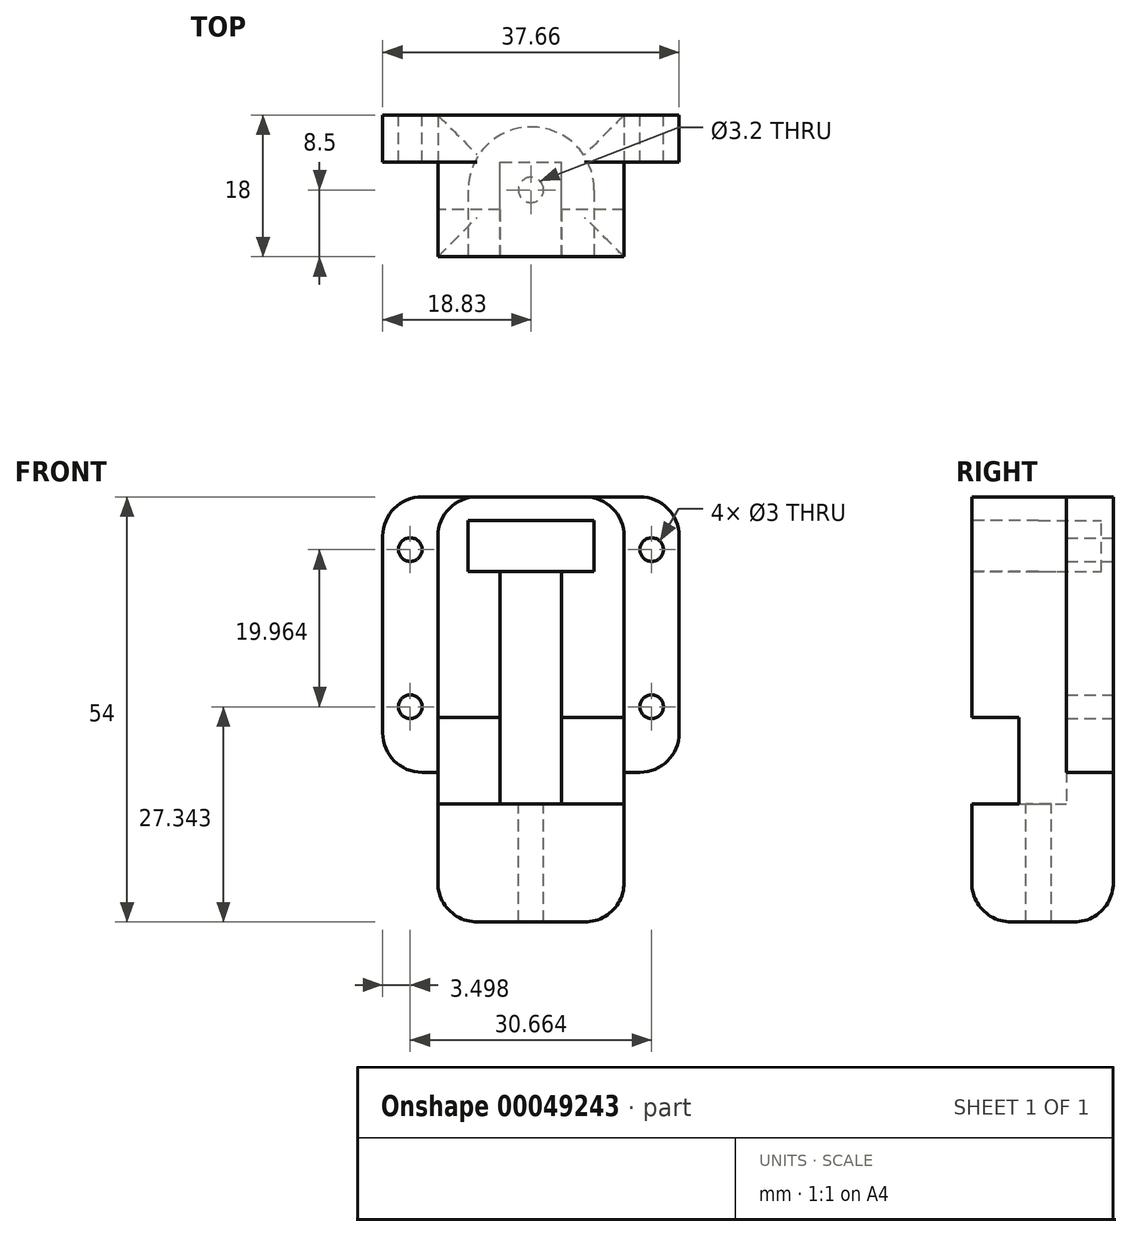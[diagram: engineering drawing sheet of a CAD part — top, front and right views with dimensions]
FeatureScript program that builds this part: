
annotation { "Feature Type Name" : "Feature", "Feature Type Description" : "" }
export const myFeature = defineFeature(function(context is Context, id is Id, definition is map)
    precondition{}
    {
        {
            var Q0;
            Q0=qCreatedBy(makeId("Top.planeOp"),FACE);
            var sketch = newSketch(context, id + "F0", { "sketchPlane" : qUnion([Q0])});
            skPoint(sketch, "E0.middle", {"position": v(0, -5.68) * mm});
            skLineSegment(sketch, "E1", {"start": v(-11.83, 0) * mm, "end": v(-11.83, -2.68) * mm});
            skLineSegment(sketch, "E2", {"start": v(-11.83, -12) * mm, "end": v(-3.9, -12) * mm});
            skLineSegment(sketch, "E3", {"start": v(-3.9, -12) * mm, "end": v(-3.9, 0) * mm});
            skLineSegment(sketch, "E4", {"start": v(-3.9, 0) * mm, "end": v(0, 0) * mm});
            skLineSegment(sketch, "E5", {"start": v(0, 6) * mm, "end": v(-11.84, 6) * mm});
            skLineSegment(sketch, "E6", {"start": v(-11.83, -2.68) * mm, "end": v(-11.83, -12) * mm});
            skLineSegment(sketch, "E7", {"start": v(-11.83, 0) * mm, "end": v(-11.83, 6) * mm});
            skLineSegment(sketch, "E8.MirrorCS", {"start": v(0, 6) * mm, "end": v(11.84, 6) * mm});
            skLineSegment(sketch, "E9.MirrorCS", {"start": v(11.83, 0) * mm, "end": v(11.83, 6) * mm});
            skLineSegment(sketch, "E10.MirrorCS", {"start": v(11.83, 0) * mm, "end": v(11.83, -2.68) * mm});
            skLineSegment(sketch, "E11.MirrorCS", {"start": v(11.83, -2.68) * mm, "end": v(11.83, -12) * mm});
            skLineSegment(sketch, "E12.MirrorCS", {"start": v(11.83, -12) * mm, "end": v(3.9, -12) * mm});
            skLineSegment(sketch, "E13.MirrorCS", {"start": v(3.9, -12) * mm, "end": v(3.9, 0) * mm});
            skLineSegment(sketch, "E14.MirrorCS", {"start": v(3.9, 0) * mm, "end": v(0, 0) * mm});
            skSolve(sketch);
        }
        {
            var Q0;
            Q0=makeQuery(id+"F0.imprint","IMPRINT",FACE,{"disambiguationData":[TD([[makeQuery(id+"F0.imprint","IMPRINT",EDGE,{"derivedFrom":sQuery(id+"F0.wireOp",EDGE,"E1")}),1.0]])]});
            extrude(context, id + "F1", {"entities" : qUnion([Q0]), "depth" : 39 * mm, "hasSecondDirection" : true, "secondDirectionOppositeDirection" : true, "secondDirectionDepth" : 15 * mm});
        }
        {
            var Q0;
            Q0=qCreatedBy(makeId("Top.planeOp"),FACE);
            var sketch = newSketch(context, id + "F2", { "sketchPlane" : qUnion([Q0])});
            skLineSegment(sketch, "E15.bottom", {"start": v(-11.83, 0) * mm, "end": v(11.83, 0) * mm});
            skLineSegment(sketch, "E15.top", {"start": v(-11.83, -12) * mm, "end": v(11.83, -12) * mm});
            skLineSegment(sketch, "E15.left", {"start": v(-11.83, 0) * mm, "end": v(-11.83, -12) * mm});
            skLineSegment(sketch, "E15.right", {"start": v(11.83, 0) * mm, "end": v(11.83, -12) * mm});
            skPoint(sketch, "E16", {"position": v(0, -3.5) * mm});
            skSolve(sketch);
        }
        {
            var Q0;
            Q0=makeQuery(id+"F2.imprint","IMPRINT",FACE,{"disambiguationData":[TD([[makeQuery(id+"F2.imprint","IMPRINT",EDGE,{"derivedFrom":sQuery(id+"F2.wireOp",EDGE,"E15.bottom")}),-1.0]])]});
            var Q1;
            Q1=makeQuery(id+"F1.opExtrude","CAP_FACE",FACE,{"disambiguationData":[OSD([sQuery(id+"F0.wireOp",EDGE,"E1"),sQuery(id+"F0.wireOp",EDGE,"E2"),sQuery(id+"F0.wireOp",EDGE,"E3"),sQuery(id+"F0.wireOp",EDGE,"E4"),sQuery(id+"F0.wireOp",EDGE,"E5"),sQuery(id+"F0.wireOp",EDGE,"E6"),sQuery(id+"F0.wireOp",EDGE,"E7"),sQuery(id+"F0.wireOp",EDGE,"E8.MirrorCS"),sQuery(id+"F0.wireOp",EDGE,"E9.MirrorCS"),sQuery(id+"F0.wireOp",EDGE,"E10.MirrorCS"),sQuery(id+"F0.wireOp",EDGE,"E11.MirrorCS"),sQuery(id+"F0.wireOp",EDGE,"E12.MirrorCS"),sQuery(id+"F0.wireOp",EDGE,"E13.MirrorCS"),sQuery(id+"F0.wireOp",EDGE,"E14.MirrorCS")])],"isStart":true});
            extrude(context, id + "F3", {"entities" : qUnion([Q0]), "operationType" : NewBodyOperationType.ADD, "endBound" : BoundingType.UP_TO_SURFACE, "oppositeDirection" : true, "endBoundEntityFace" : qUnion([Q1]), "depth" : 25 * mm});
        }
        {
            var Q0;
            Q0=sQuery(id+"F2.wireOp",VERTEX,"E16");
            var Q1;
            Q1=makeQuery(id+"F1.opExtrude","SWEPT_BODY",BODY,{"disambiguationData":[OSD([sQuery(id+"F0.wireOp",EDGE,"E1"),sQuery(id+"F0.wireOp",EDGE,"E2"),sQuery(id+"F0.wireOp",EDGE,"E3"),sQuery(id+"F0.wireOp",EDGE,"E4"),sQuery(id+"F0.wireOp",EDGE,"E5"),sQuery(id+"F0.wireOp",EDGE,"E6"),sQuery(id+"F0.wireOp",EDGE,"E7"),sQuery(id+"F0.wireOp",EDGE,"E8.MirrorCS"),sQuery(id+"F0.wireOp",EDGE,"E9.MirrorCS"),sQuery(id+"F0.wireOp",EDGE,"E10.MirrorCS"),sQuery(id+"F0.wireOp",EDGE,"E11.MirrorCS"),sQuery(id+"F0.wireOp",EDGE,"E12.MirrorCS"),sQuery(id+"F0.wireOp",EDGE,"E13.MirrorCS"),sQuery(id+"F0.wireOp",EDGE,"E14.MirrorCS")])]});
            hole(context, id + "F4", {"style" : HoleStyle.SIMPLE, "endStyle" : HoleEndStyle.THROUGH, "holeDiameter" : 3.2 * mm, "locations" : qUnion([Q0]), "scope" : qUnion([Q1]), "isTappedThrough" : true});
        }
        {
            var Q0;
            Q0=makeQuery(id+"F3.boolean.opBoolean","MERGE",FACE,{"derivedFrom":[makeQuery(id+"F1.opExtrude","SWEPT_FACE",FACE,{"disambiguationData":[OSD([sQuery(id+"F0.wireOp",EDGE,"E2")])]}),makeQuery(id+"F1.opExtrude","SWEPT_FACE",FACE,{"disambiguationData":[OSD([sQuery(id+"F0.wireOp",EDGE,"E12.MirrorCS")])]}),makeQuery(id+"F3.opExtrude","SWEPT_FACE",FACE,{"disambiguationData":[OSD([sQuery(id+"F2.wireOp",EDGE,"E15.top")])]})]});
            var sketch = newSketch(context, id + "F5", { "sketchPlane" : qUnion([Q0])});
            skLineSegment(sketch, "E17.bottom", {"start": v(11.83, 0) * mm, "end": v(-11.83, 0) * mm});
            skLineSegment(sketch, "E17.top", {"start": v(11.83, 11) * mm, "end": v(-11.83, 11) * mm});
            skLineSegment(sketch, "E17.left", {"start": v(11.83, 0) * mm, "end": v(11.83, 11) * mm});
            skLineSegment(sketch, "E17.right", {"start": v(-11.83, 0) * mm, "end": v(-11.83, 11) * mm});
            skSolve(sketch);
        }
        {
            var Q0;
            {var subQ4=sQuery(id+"F5.wireOp",EDGE,"E17.left");Q0=makeQuery(id+"F5.imprint","IMPRINT",FACE,{"disambiguationData":[TD([[makeQuery(id+"F5.imprint","IMPRINT",EDGE,{"derivedFrom":subQ4}),-1.0]])]});}
            var Q1;
            {var subQ4=sQuery(id+"F5.wireOp",EDGE,"E17.right");Q1=makeQuery(id+"F5.imprint","IMPRINT",FACE,{"disambiguationData":[TD([[makeQuery(id+"F5.imprint","IMPRINT",EDGE,{"derivedFrom":subQ4}),1.0]])]});}
            var Q2;
            Q2=makeQuery(id+"F1.opExtrude","SWEPT_FACE",FACE,{"disambiguationData":[OSD([sQuery(id+"F0.wireOp",EDGE,"E4"),sQuery(id+"F0.wireOp",EDGE,"E14.MirrorCS")])]});
            extrude(context, id + "F6", {"entities" : qUnion([Q0, Q1]), "operationType" : NewBodyOperationType.REMOVE, "oppositeDirection" : true, "endBoundEntityFace" : qUnion([Q2]), "depth" : 6 * mm});
        }
        {
            var Q0;
            Q0=qCreatedBy(makeId("Top.planeOp"),FACE);
            cPlane(context, id + "F7", {"entities" : qUnion([Q0]), "cplaneType" : CPlaneType.OFFSET, "offset" : 36 * mm, "width" : 150 * mm, "height" : 150 * mm});
        }
        {
            var Q0;
            Q0=qCreatedBy(id+"F7.planeOp",FACE);
            var sketch = newSketch(context, id + "F8", { "sketchPlane" : qUnion([Q0])});
            skArc(sketch, "E18", {"start": v(8.03, -3.5) * mm, "mid": v(0.03, 4.5) * mm, "end": v(-7.97, -3.5) * mm});
            skLineSegment(sketch, "E19.0", {"start": v(-7.97, -12) * mm, "end": v(3.9, -12) * mm});
            skLineSegment(sketch, "E20.0", {"start": v(8.03, -12) * mm, "end": v(3.9, -12) * mm});
            skLineSegment(sketch, "E21", {"start": v(8.03, -3.5) * mm, "end": v(8.03, -12) * mm});
            skLineSegment(sketch, "E22", {"start": v(-7.97, -3.5) * mm, "end": v(-7.97, -12) * mm});
            skPoint(sketch, "E23.orphan", {"position": v(-3.9, -12) * mm});
            skPoint(sketch, "E24.orphan", {"position": v(11.83, -12) * mm});
            skPoint(sketch, "E25.orphan", {"position": v(-11.83, -12) * mm});
            skSolve(sketch);
        }
        {
            var Q0;
            Q0=makeQuery(id+"F8.imprint","IMPRINT",FACE,{"disambiguationData":[TD([[makeQuery(id+"F8.imprint","IMPRINT",EDGE,{"derivedFrom":sQuery(id+"F8.wireOp",EDGE,"E18")}),1.0]])]});
            extrude(context, id + "F9", {"entities" : qUnion([Q0]), "operationType" : NewBodyOperationType.REMOVE, "oppositeDirection" : true, "depth" : 6.5 * mm});
        }
        {
            var Q0;
            {var subQ0=sQuery(id+"F0.wireOp",EDGE,"E14.MirrorCS");var subQ2=sQuery(id+"F0.wireOp",EDGE,"E4");Q0=makeQuery(id+"F9.boolean.opBoolean","SPLIT",FACE,{"disambiguationData":[TD([makeQuery(id+"F9.opExtrude","CAP_FACE",FACE,{"disambiguationData":[OSD([sQuery(id+"F8.wireOp",EDGE,"E18"),sQuery(id+"F8.wireOp",EDGE,"E19.0"),sQuery(id+"F8.wireOp",EDGE,"E20.0"),sQuery(id+"F8.wireOp",EDGE,"E21"),sQuery(id+"F8.wireOp",EDGE,"E22")])],"isStart":true})])],"derivedFrom":makeQuery(id+"F1.opExtrude","SWEPT_FACE",FACE,{"disambiguationData":[OSD([subQ2,subQ0])]})});}
            var Q1;
            {var subQ0=sQuery(id+"F0.wireOp",EDGE,"E12.MirrorCS");var subQ3=sQuery(id+"F0.wireOp",EDGE,"E3");var subQ4=sQuery(id+"F0.wireOp",EDGE,"E2");Q1=makeQuery(id+"F6.boolean.opBoolean","SPLIT",FACE,{"disambiguationData":[TD([makeQuery(id+"F1.opExtrude","SWEPT_FACE",FACE,{"disambiguationData":[OSD([subQ3])]})])],"derivedFrom":makeQuery(id+"F3.boolean.opBoolean","MERGE",FACE,{"derivedFrom":[makeQuery(id+"F1.opExtrude","SWEPT_FACE",FACE,{"disambiguationData":[OSD([subQ4])]}),makeQuery(id+"F1.opExtrude","SWEPT_FACE",FACE,{"disambiguationData":[OSD([subQ0])]}),makeQuery(id+"F3.opExtrude","SWEPT_FACE",FACE,{"disambiguationData":[OSD([sQuery(id+"F2.wireOp",EDGE,"E15.top")])]})]})});}
            extrude(context, id + "F10", {"entities" : qUnion([Q0]), "operationType" : NewBodyOperationType.ADD, "endBound" : BoundingType.UP_TO_SURFACE, "endBoundEntityFace" : qUnion([Q1]), "depth" : 25 * mm});
        }
        {
            var Q0;
            Q0=makeQuery(id+"F1.opExtrude","SWEPT_FACE",FACE,{"disambiguationData":[OSD([sQuery(id+"F0.wireOp",EDGE,"E1"),sQuery(id+"F0.wireOp",EDGE,"E6"),sQuery(id+"F0.wireOp",EDGE,"E7")])]});
            var sketch = newSketch(context, id + "F11", { "sketchPlane" : qUnion([Q0])});
            skLineSegment(sketch, "E26.bottom", {"start": v(-6, 39) * mm, "end": v(0, 39) * mm});
            skLineSegment(sketch, "E26.top", {"start": v(-6, 4) * mm, "end": v(0, 4) * mm});
            skLineSegment(sketch, "E26.left", {"start": v(-6, 39) * mm, "end": v(-6, 4) * mm});
            skLineSegment(sketch, "E26.right", {"start": v(0, 39) * mm, "end": v(0, 4) * mm});
            skSolve(sketch);
        }
        {
            var Q0;
            Q0=makeQuery(id+"F11.imprint","IMPRINT",FACE,{"disambiguationData":[TD([[makeQuery(id+"F11.imprint","IMPRINT",EDGE,{"derivedFrom":sQuery(id+"F11.wireOp",EDGE,"E26.bottom")}),1.0]])]});
            extrude(context, id + "F12", {"entities" : qUnion([Q0]), "operationType" : NewBodyOperationType.ADD, "depth" : 7 * mm});
        }
        {
            var Q0;
            Q0=makeQuery(id+"F1.opExtrude","SWEPT_FACE",FACE,{"disambiguationData":[OSD([sQuery(id+"F0.wireOp",EDGE,"E9.MirrorCS"),sQuery(id+"F0.wireOp",EDGE,"E10.MirrorCS"),sQuery(id+"F0.wireOp",EDGE,"E11.MirrorCS")])]});
            var sketch = newSketch(context, id + "F13", { "sketchPlane" : qUnion([Q0])});
            skLineSegment(sketch, "E27.bottom", {"start": v(6, 39) * mm, "end": v(0, 39) * mm});
            skLineSegment(sketch, "E27.top", {"start": v(6, 4) * mm, "end": v(0, 4) * mm});
            skLineSegment(sketch, "E27.left", {"start": v(6, 39) * mm, "end": v(6, 4) * mm});
            skLineSegment(sketch, "E27.right", {"start": v(0, 39) * mm, "end": v(0, 4) * mm});
            skSolve(sketch);
        }
        {
            var Q0;
            Q0=makeQuery(id+"F13.imprint","IMPRINT",FACE,{"disambiguationData":[TD([[makeQuery(id+"F13.imprint","IMPRINT",EDGE,{"derivedFrom":sQuery(id+"F13.wireOp",EDGE,"E27.bottom")}),1.0]])]});
            extrude(context, id + "F14", {"entities" : qUnion([Q0]), "operationType" : NewBodyOperationType.ADD, "depth" : 7 * mm});
        }
        {
            var Q0;
            Q0=makeQuery(id+"F12.opExtrude","CAP_EDGE",EDGE,{"disambiguationData":[OSD([sQuery(id+"F11.wireOp",EDGE,"E26.bottom")])],"isStart":false});
            var Q1;
            Q1=makeQuery(id+"F12.opExtrude","CAP_EDGE",EDGE,{"disambiguationData":[OSD([sQuery(id+"F11.wireOp",EDGE,"E26.top")])],"isStart":false});
            var Q2;
            Q2=makeQuery(id+"F14.opExtrude","CAP_EDGE",EDGE,{"disambiguationData":[OSD([sQuery(id+"F13.wireOp",EDGE,"E27.top")])],"isStart":false});
            var Q3;
            Q3=makeQuery(id+"F14.opExtrude","CAP_EDGE",EDGE,{"disambiguationData":[OSD([sQuery(id+"F13.wireOp",EDGE,"E27.bottom")])],"isStart":false});
            var Q4;
            Q4=makeQuery(id+"F1.opExtrude","CAP_EDGE",EDGE,{"disambiguationData":[OSD([sQuery(id+"F0.wireOp",EDGE,"E1"),sQuery(id+"F0.wireOp",EDGE,"E6"),sQuery(id+"F0.wireOp",EDGE,"E7")])],"isStart":false});
            var Q5;
            Q5=makeQuery(id+"F1.opExtrude","CAP_EDGE",EDGE,{"disambiguationData":[OSD([sQuery(id+"F0.wireOp",EDGE,"E9.MirrorCS"),sQuery(id+"F0.wireOp",EDGE,"E10.MirrorCS"),sQuery(id+"F0.wireOp",EDGE,"E11.MirrorCS")])],"isStart":false});
            fillet(context, id + "F15", {"entities" : qUnion([Q0, Q1, Q2, Q3, Q4, Q5]), "radius" : 5 * mm, "tangentPropagation" : true, "allowEdgeOverflow" : false});
        }
        {
            var Q0;
            Q0=makeQuery(id+"F1.opExtrude","CAP_EDGE",EDGE,{"disambiguationData":[OSD([sQuery(id+"F0.wireOp",EDGE,"E1"),sQuery(id+"F0.wireOp",EDGE,"E6"),sQuery(id+"F0.wireOp",EDGE,"E7")])],"isStart":true});
            var Q1;
            Q1=makeQuery(id+"F3.boolean.opBoolean","MERGE",EDGE,{"derivedFrom":[makeQuery(id+"F1.opExtrude","CAP_EDGE",EDGE,{"disambiguationData":[OSD([sQuery(id+"F0.wireOp",EDGE,"E2")])],"isStart":true}),makeQuery(id+"F1.opExtrude","CAP_EDGE",EDGE,{"disambiguationData":[OSD([sQuery(id+"F0.wireOp",EDGE,"E12.MirrorCS")])],"isStart":true}),makeQuery(id+"F3.opExtrude","CAP_EDGE",EDGE,{"disambiguationData":[OSD([sQuery(id+"F2.wireOp",EDGE,"E15.top")])],"isStart":false})]});
            var Q2;
            Q2=makeQuery(id+"F1.opExtrude","CAP_EDGE",EDGE,{"disambiguationData":[OSD([sQuery(id+"F0.wireOp",EDGE,"E9.MirrorCS"),sQuery(id+"F0.wireOp",EDGE,"E10.MirrorCS"),sQuery(id+"F0.wireOp",EDGE,"E11.MirrorCS")])],"isStart":true});
            var Q3;
            Q3=makeQuery(id+"F1.opExtrude","CAP_EDGE",EDGE,{"disambiguationData":[OSD([sQuery(id+"F0.wireOp",EDGE,"E5"),sQuery(id+"F0.wireOp",EDGE,"E8.MirrorCS")])],"isStart":true});
            fillet(context, id + "F16", {"entities" : qUnion([Q0, Q1, Q2, Q3]), "radius" : 5 * mm, "tangentPropagation" : true, "allowEdgeOverflow" : false});
        }
        {
            var Q0;
            Q0=makeQuery(id+"F14.boolean.opBoolean","MERGE",FACE,{"derivedFrom":[makeQuery(id+"F12.boolean.opBoolean","MERGE",FACE,{"derivedFrom":[makeQuery(id+"F1.opExtrude","SWEPT_FACE",FACE,{"disambiguationData":[OSD([sQuery(id+"F0.wireOp",EDGE,"E5"),sQuery(id+"F0.wireOp",EDGE,"E8.MirrorCS")])]}),makeQuery(id+"F12.opExtrude","SWEPT_FACE",FACE,{"disambiguationData":[OSD([sQuery(id+"F11.wireOp",EDGE,"E26.left")])]})]}),makeQuery(id+"F14.opExtrude","SWEPT_FACE",FACE,{"disambiguationData":[OSD([sQuery(id+"F13.wireOp",EDGE,"E27.left")])]})]});
            var sketch = newSketch(context, id + "F17", { "sketchPlane" : qUnion([Q0])});
            skLineSegment(sketch, "E28", {"start": v(-11.83, 4) * mm, "end": v(-11.83, 39) * mm, "construction": true});
            skLineSegment(sketch, "E29", {"start": v(-11.83, 32.3) * mm, "end": v(-18.83, 32.3) * mm, "construction": true});
            skLineSegment(sketch, "E30", {"start": v(-11.83, 12.34) * mm, "end": v(-18.83, 12.34) * mm, "construction": true});
            skPoint(sketch, "E31", {"position": v(-15.33, 32.3) * mm});
            skPoint(sketch, "E32", {"position": v(-15.33, 12.34) * mm});
            skPoint(sketch, "E33.MirrorP", {"position": v(15.33, 12.34) * mm});
            skPoint(sketch, "E34.MirrorP", {"position": v(15.33, 32.3) * mm});
            skSolve(sketch);
        }
        {
            var Q0;
            Q0=sQuery(id+"F17.wireOp",VERTEX,"E31");
            var Q1;
            Q1=sQuery(id+"F17.wireOp",VERTEX,"E32");
            var Q2;
            Q2=sQuery(id+"F17.wireOp",VERTEX,"E33.MirrorP");
            var Q3;
            Q3=sQuery(id+"F17.wireOp",VERTEX,"E34.MirrorP");
            var Q4;
            Q4=makeQuery(id+"F1.opExtrude","SWEPT_BODY",BODY,{"disambiguationData":[OSD([sQuery(id+"F0.wireOp",EDGE,"E1"),sQuery(id+"F0.wireOp",EDGE,"E2"),sQuery(id+"F0.wireOp",EDGE,"E3"),sQuery(id+"F0.wireOp",EDGE,"E4"),sQuery(id+"F0.wireOp",EDGE,"E5"),sQuery(id+"F0.wireOp",EDGE,"E6"),sQuery(id+"F0.wireOp",EDGE,"E7"),sQuery(id+"F0.wireOp",EDGE,"E8.MirrorCS"),sQuery(id+"F0.wireOp",EDGE,"E9.MirrorCS"),sQuery(id+"F0.wireOp",EDGE,"E10.MirrorCS"),sQuery(id+"F0.wireOp",EDGE,"E11.MirrorCS"),sQuery(id+"F0.wireOp",EDGE,"E12.MirrorCS"),sQuery(id+"F0.wireOp",EDGE,"E13.MirrorCS"),sQuery(id+"F0.wireOp",EDGE,"E14.MirrorCS")])]});
            hole(context, id + "F18", {"style" : HoleStyle.SIMPLE, "endStyle" : HoleEndStyle.THROUGH, "holeDiameter" : 3 * mm, "locations" : qUnion([Q0, Q1, Q2, Q3]), "scope" : qUnion([Q4]), "isTappedThrough" : true});
        }
    });
